# Revit family: Safety-Equipment_Door-Frame-Protection_Omega-Industrial_Goal-Post-Door-Guard
name_source: partatom
category: Generic Models
units: mm (PartAtom-declared; Revit-internal decimal feet)

## family parameters
Always vertical = Yes
Can host rebar = No
Classification Number = 23.30.80.17
Cut with Voids When Loaded = No
Maintain Annotation Orientation = No
Part Type = Normal
Room Calculation Point = No
Round Connector Dimension = Use Diameter
Shared = No
Work Plane-Based = Yes

## types (4) — shared parameters
Assembly Code = E1090
Base Plate Material = Omega_1/2 in Steel
Default Elevation = 4' - 0"
Description = Goal Post Style Overhead Door Guard
Expected Lifespan (Years) = 25
Guard Material = Omega_7 Ga. Steel
Installation Phase = Industrial Safety Equipment
Keynote = 41 67 19
Manufacturer = Omega Industrial Products, Inc.
Manufacturer Fax = 262-284-4199
Manufacturer Website = https://www.omegaindl.com
Product Data = https://www.arcat.com
Product Properties = https://www.omegaindl.com
Revision = R0_06-2018
Sales Information = https://www.omegaindl.com
Send Message = https://www.omegaindl.com
Specification = https://www.arcat.com
URL = https://www.arcat.com
Unit Depth = 0' - 4"
zero-valued in all types: Maintenance Schedule (Months), Warranty Duration (Years)

## per-type parameters (varying)
| type | Model | Unit Height | Unit Width |
| 96in x 96in | OM6100-96X96 | 8' - 0" | 8' - 0" |
| 120in x 120in | OM6100-120X120 | 10' - 0" | 10' - 0" |
| 96in x 120in | OM6100-96X120 | 10' - 0" | 8' - 0" |
| 144in x 144in | OM6100-144X144 | 12' - 0" | 12' - 0" |

## geometry (parser evidence)
native form markers: Blend x48, Sweep x2
no freeform markers — native parametric forms only
